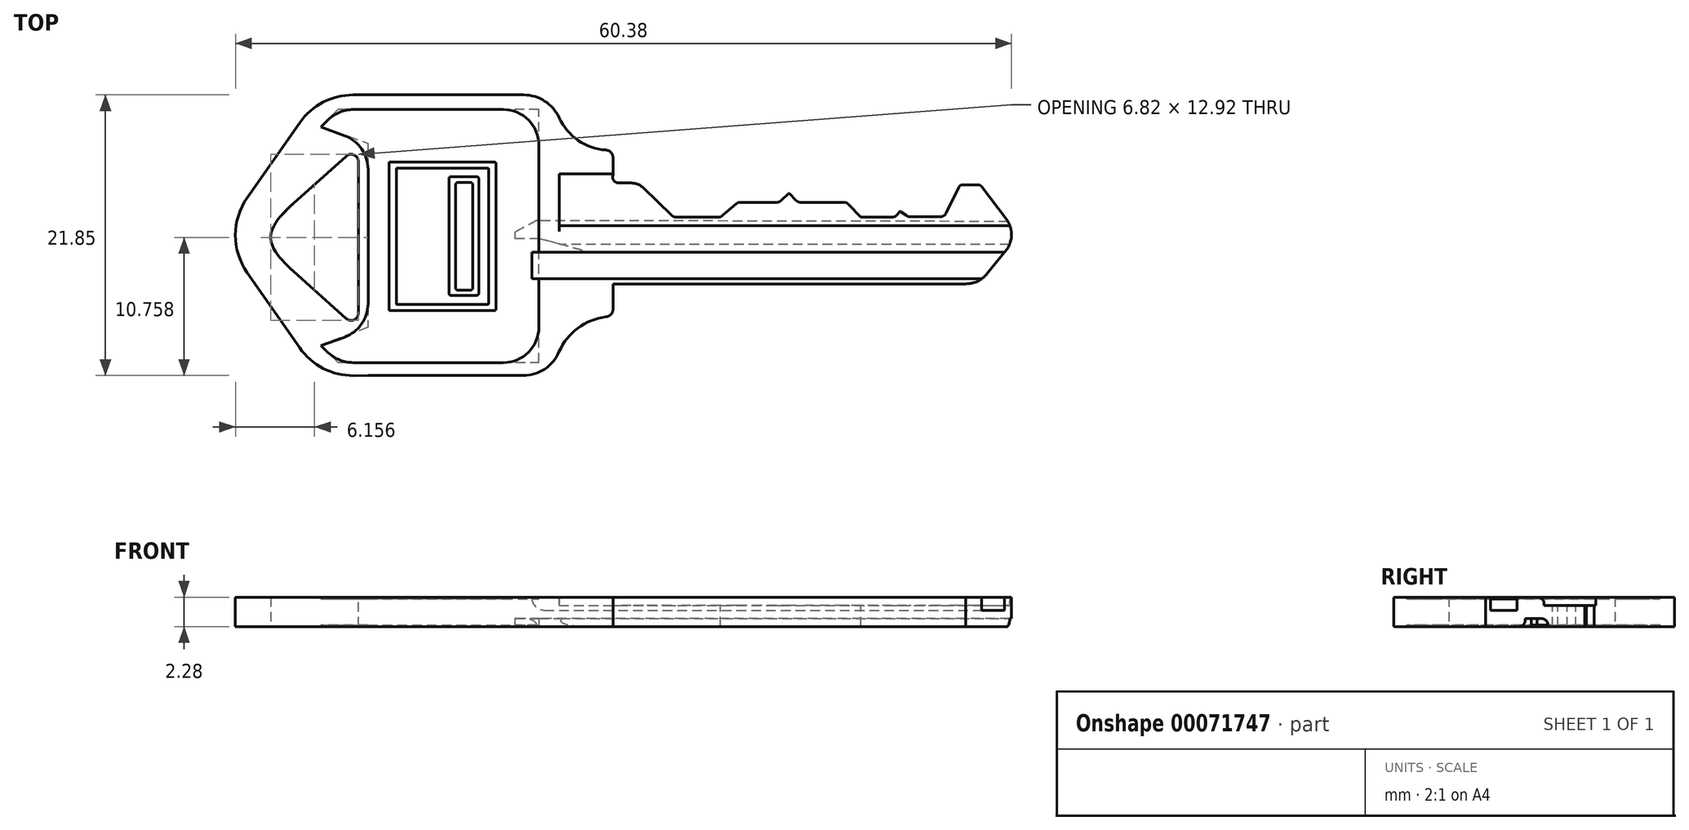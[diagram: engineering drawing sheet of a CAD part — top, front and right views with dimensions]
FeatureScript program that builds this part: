
annotation { "Feature Type Name" : "Feature", "Feature Type Description" : "" }
export const myFeature = defineFeature(function(context is Context, id is Id, definition is map)
    precondition{}
    {
        {
            var Q0;
            Q0=qCreatedBy(makeId("Top.planeOp"),FACE);
            var sketch = newSketch(context, id + "F0", { "sketchPlane" : qUnion([Q0])});
            skLineSegment(sketch, "E0.bottom", {"start": v(-49.06, 40.34) * mm, "end": v(-34.58, 40.34) * mm});
            skLineSegment(sketch, "E0.top", {"start": v(-49.06, 18.5) * mm, "end": v(-34.58, 18.5) * mm});
            skLineSegment(sketch, "E0.left", {"start": v(-49.06, 40.34) * mm, "end": v(-49.06, 18.5) * mm});
            skLineSegment(sketch, "E0.right", {"start": v(-34.58, 40.34) * mm, "end": v(-34.58, 18.5) * mm});
            skLineSegment(sketch, "E1.bottom", {"start": v(-34.58, 33.5) * mm, "end": v(-2.57, 33.5) * mm});
            skLineSegment(sketch, "E1.top", {"start": v(-34.58, 25.63) * mm, "end": v(-2.57, 25.63) * mm});
            skLineSegment(sketch, "E1.left", {"start": v(-34.58, 33.5) * mm, "end": v(-34.58, 25.63) * mm});
            skLineSegment(sketch, "E1.right", {"start": v(-2.57, 33.5) * mm, "end": v(-2.57, 25.63) * mm});
            skLineSegment(sketch, "E2.bottom", {"start": v(-34.58, 36.05) * mm, "end": v(-30, 36.05) * mm});
            skLineSegment(sketch, "E2.top", {"start": v(-34.58, 23.1) * mm, "end": v(-30, 23.1) * mm});
            skLineSegment(sketch, "E2.left", {"start": v(-34.58, 36.05) * mm, "end": v(-34.58, 23.1) * mm});
            skLineSegment(sketch, "E2.right", {"start": v(-30, 36.05) * mm, "end": v(-30, 23.1) * mm});
            skArc(sketch, "E3", {"start": v(-34.58, 40.34) * mm, "mid": v(-33.22, 37.2) * mm, "end": v(-30, 36.05) * mm});
            skArc(sketch, "E4", {"start": v(-30, 23.1) * mm, "mid": v(-33.25, 21.74) * mm, "end": v(-34.58, 18.5) * mm});
            skPoint(sketch, "E5", {"position": v(-30, 33.5) * mm});
            skPoint(sketch, "E6", {"position": v(-30, 25.63) * mm});
            skLineSegment(sketch, "E7", {"start": v(-49.06, 29.42) * mm, "end": v(-2.57, 29.42) * mm});
            skPoint(sketch, "E8", {"position": v(-30, 29.42) * mm});
            skLineSegment(sketch, "E9", {"start": v(-49.06, 40.34) * mm, "end": v(-52.87, 40.34) * mm});
            skLineSegment(sketch, "E10", {"start": v(-52.87, 40.34) * mm, "end": v(-60.5, 29.42) * mm});
            skLineSegment(sketch, "E11", {"start": v(-60.5, 29.42) * mm, "end": v(-52.87, 18.47) * mm});
            skLineSegment(sketch, "E12", {"start": v(-52.87, 18.47) * mm, "end": v(-49.06, 18.5) * mm});
            skLineSegment(sketch, "E13", {"start": v(-2.57, 33.5) * mm, "end": v(-1.57, 33.5) * mm});
            skLineSegment(sketch, "E14", {"start": v(-1.57, 33.5) * mm, "end": v(1.56, 29.42) * mm});
            skLineSegment(sketch, "E15", {"start": v(1.56, 29.42) * mm, "end": v(-1.57, 25.62) * mm});
            skLineSegment(sketch, "E16", {"start": v(-1.57, 25.62) * mm, "end": v(-2.57, 25.63) * mm});
            skSolve(sketch);
        }
        {
            var Q0;
            Q0=makeQuery(id+"F0.imprint","IMPRINT",FACE,{"disambiguationData":[TD([[makeQuery(id+"F0.imprint","IMPRINT",EDGE,{"derivedFrom":sQuery(id+"F0.wireOp",EDGE,"E1.bottom")}),-1.0]])]});
            var Q1;
            {var subQ0=sQuery(id+"F0.wireOp",EDGE,"E3");var subQ3=sQuery(id+"F0.wireOp",EDGE,"E2.bottom");var subQ5=makeQuery(id+"F0.imprint","INTERSECT",VERTEX,{"derivedFrom":[subQ3,subQ0]});Q1=makeQuery(id+"F0.imprint","IMPRINT",FACE,{"disambiguationData":[TD([[makeQuery(id+"F0.imprint","IMPRINT",EDGE,{"disambiguationData":[TD([[subQ5,1.0]])],"derivedFrom":subQ3}),1.0]])]});}
            var Q2;
            {var subQ4=sQuery(id+"F0.wireOp",EDGE,"E1.bottom");var subQ6=sQuery(id+"F0.wireOp",EDGE,"E2.left");var subQ7=makeQuery(id+"F0.imprint","INTERSECT",VERTEX,{"derivedFrom":[subQ4,subQ6]});Q2=makeQuery(id+"F0.imprint","IMPRINT",FACE,{"disambiguationData":[TD([[makeQuery(id+"F0.imprint","IMPRINT",EDGE,{"disambiguationData":[TD([[subQ7,-1.0]])],"derivedFrom":subQ4}),1.0]])]});}
            var Q3;
            {var subQ5=sQuery(id+"F0.wireOp",EDGE,"E2.top");Q3=makeQuery(id+"F0.imprint","IMPRINT",FACE,{"disambiguationData":[TD([[makeQuery(id+"F0.imprint","IMPRINT",EDGE,{"derivedFrom":subQ5}),1.0]])]});}
            var Q4;
            {var subQ0=sQuery(id+"F0.wireOp",EDGE,"E2.top");Q4=makeQuery(id+"F0.imprint","IMPRINT",FACE,{"disambiguationData":[TD([[makeQuery(id+"F0.imprint","IMPRINT",EDGE,{"derivedFrom":subQ0}),-1.0]])]});}
            var Q5;
            {var subQ0=sQuery(id+"F0.wireOp",EDGE,"3a7dfe4d-6823-4ebe-8630-0b1af203f991.3");Q5=makeQuery(id+"F0.imprint","IMPRINT",FACE,{"disambiguationData":[TD([[makeQuery(id+"F0.imprint","IMPRINT",EDGE,{"derivedFrom":subQ0}),1.0]])]});}
            var Q6;
            {var subQ0=sQuery(id+"F0.wireOp",EDGE,"E0.left");Q6=makeQuery(id+"F0.imprint","IMPRINT",FACE,{"disambiguationData":[TD([[makeQuery(id+"F0.imprint","IMPRINT",EDGE,{"derivedFrom":subQ0}),-1.0]])]});}
            var Q7;
            {var subQ4=sQuery(id+"F0.wireOp",EDGE,"E0.left");Q7=makeQuery(id+"F0.imprint","IMPRINT",FACE,{"disambiguationData":[TD([[makeQuery(id+"F0.imprint","IMPRINT",EDGE,{"derivedFrom":subQ4}),1.0]])]});}
            var Q8;
            {var subQ9=sQuery(id+"F0.wireOp",EDGE,"E0.top");Q8=makeQuery(id+"F0.imprint","IMPRINT",FACE,{"disambiguationData":[TD([[makeQuery(id+"F0.imprint","IMPRINT",EDGE,{"derivedFrom":subQ9}),1.0]])]});}
            var Q9;
            {var subQ0=sQuery(id+"F0.wireOp",EDGE,"E2.left");var subQ1=sQuery(id+"F0.wireOp",EDGE,"E1.top");var subQ2=makeQuery(id+"F0.imprint","INTERSECT",VERTEX,{"derivedFrom":[subQ1,subQ0]});Q9=makeQuery(id+"F0.imprint","IMPRINT",FACE,{"disambiguationData":[TD([[makeQuery(id+"F0.imprint","IMPRINT",EDGE,{"disambiguationData":[TD([[subQ2,-1.0]])],"derivedFrom":subQ1}),1.0]])]});}
            var Q10;
            {var subQ0=sQuery(id+"F0.wireOp",EDGE,"E1.right");var subQ1=sQuery(id+"F0.wireOp",EDGE,"E1.top");var subQ2=makeQuery(id+"F0.imprint","INTERSECT",VERTEX,{"derivedFrom":[subQ1,subQ0]});Q10=makeQuery(id+"F0.imprint","IMPRINT",FACE,{"disambiguationData":[TD([[makeQuery(id+"F0.imprint","IMPRINT",EDGE,{"disambiguationData":[TD([[subQ2,1.0]])],"derivedFrom":subQ1}),1.0]])]});}
            var Q11;
            {var subQ3=sQuery(id+"F0.wireOp",EDGE,"E13");Q11=makeQuery(id+"F0.imprint","IMPRINT",FACE,{"disambiguationData":[TD([[makeQuery(id+"F0.imprint","IMPRINT",EDGE,{"derivedFrom":subQ3}),-1.0]])]});}
            extrude(context, id + "F1", {"entities" : qUnion([Q0, Q1, Q2, Q3, Q4, Q5, Q6, Q7, Q8, Q9, Q10, Q11]), "endBound" : BoundingType.SYMMETRIC, "depth" : 2.3 * mm});
        }
        {
            var Q0;
            Q0=makeQuery(id+"F1.opExtrude","CAP_FACE",FACE,{"disambiguationData":[OSD([sQuery(id+"F0.wireOp",EDGE,"E0.bottom"),sQuery(id+"F0.wireOp",EDGE,"E0.top"),sQuery(id+"F0.wireOp",EDGE,"E1.bottom"),sQuery(id+"F0.wireOp",EDGE,"E1.top"),sQuery(id+"F0.wireOp",EDGE,"E1.right"),sQuery(id+"F0.wireOp",EDGE,"E2.right"),sQuery(id+"F0.wireOp",EDGE,"E3"),sQuery(id+"F0.wireOp",EDGE,"E4"),sQuery(id+"F0.wireOp",EDGE,"E9"),sQuery(id+"F0.wireOp",EDGE,"E10"),sQuery(id+"F0.wireOp",EDGE,"E11"),sQuery(id+"F0.wireOp",EDGE,"E12")])],"isStart":false});
            var sketch = newSketch(context, id + "F2", { "sketchPlane" : qUnion([Q0])});
            skLineSegment(sketch, "E17", {"start": v(-57.81, 29.25) * mm, "end": v(-49.81, 22.07) * mm});
            skLineSegment(sketch, "E18", {"start": v(-49.81, 22.07) * mm, "end": v(-49.81, 36.43) * mm});
            skLineSegment(sketch, "E19", {"start": v(-49.81, 36.43) * mm, "end": v(-57.81, 29.25) * mm});
            skPoint(sketch, "E20", {"position": v(-49.81, 29.25) * mm});
            skSolve(sketch);
        }
        {
            var Q0;
            Q0=makeQuery(id+"F1.opExtrude","SWEPT_EDGE",EDGE,{"disambiguationData":[OSD([sQuery(id+"F0.wireOp",EDGE,"E11"),sQuery(id+"F0.wireOp",EDGE,"E12")])]});
            var Q1;
            Q1=makeQuery(id+"F1.opExtrude","SWEPT_EDGE",EDGE,{"disambiguationData":[OSD([sQuery(id+"F0.wireOp",EDGE,"E9"),sQuery(id+"F0.wireOp",EDGE,"E10")])]});
            var Q2;
            Q2=makeQuery(id+"F1.opExtrude","SWEPT_EDGE",EDGE,{"disambiguationData":[OSD([sQuery(id+"F0.wireOp",EDGE,"E10"),sQuery(id+"F0.wireOp",EDGE,"E11")])]});
            fillet(context, id + "F3", {"entities" : qUnion([Q0, Q1, Q2]), "radius" : 5.08 * mm, "tangentPropagation" : true, "allowEdgeOverflow" : false});
        }
        {
            var Q0;
            Q0=makeQuery(id+"F1.opExtrude","SWEPT_EDGE",EDGE,{"disambiguationData":[OSD([sQuery(id+"F0.wireOp",EDGE,"E0.bottom"),sQuery(id+"F0.wireOp",EDGE,"E0.right"),sQuery(id+"F0.wireOp",EDGE,"E3")])]});
            var Q1;
            Q1=makeQuery(id+"F1.opExtrude","SWEPT_EDGE",EDGE,{"disambiguationData":[OSD([sQuery(id+"F0.wireOp",EDGE,"E0.top"),sQuery(id+"F0.wireOp",EDGE,"E0.right"),sQuery(id+"F0.wireOp",EDGE,"E4")])]});
            fillet(context, id + "F4", {"entities" : qUnion([Q0, Q1]), "radius" : 3.05 * mm, "tangentPropagation" : true, "allowEdgeOverflow" : false});
        }
        {
            var Q0;
            Q0=makeQuery(id+"F1.opExtrude","SWEPT_EDGE",EDGE,{"disambiguationData":[OSD([sQuery(id+"F0.wireOp",EDGE,"E2.bottom"),sQuery(id+"F0.wireOp",EDGE,"E2.right"),sQuery(id+"F0.wireOp",EDGE,"E3")])]});
            var Q1;
            Q1=makeQuery(id+"F1.opExtrude","SWEPT_EDGE",EDGE,{"disambiguationData":[OSD([sQuery(id+"F0.wireOp",EDGE,"E2.top"),sQuery(id+"F0.wireOp",EDGE,"E2.right"),sQuery(id+"F0.wireOp",EDGE,"E4")])]});
            fillet(context, id + "F5", {"entities" : qUnion([Q0, Q1]), "radius" : 0.6 * mm, "tangentPropagation" : true, "allowEdgeOverflow" : false});
        }
        {
            var Q0;
            Q0=makeQuery(id+"F2.imprint","IMPRINT",FACE,{"disambiguationData":[TD([[makeQuery(id+"F2.imprint","IMPRINT",EDGE,{"derivedFrom":sQuery(id+"F2.wireOp",EDGE,"E17")}),1.0]])]});
            extrude(context, id + "F6", {"entities" : qUnion([Q0]), "operationType" : NewBodyOperationType.REMOVE, "endBound" : BoundingType.THROUGH_ALL, "oppositeDirection" : true, "depth" : 9.1 * mm});
        }
        {
            var Q0;
            Q0=makeQuery(id+"F6.boolean.opBoolean","COPY",EDGE,{"derivedFrom":makeQuery(id+"F6.opExtrude","SWEPT_EDGE",EDGE,{"disambiguationData":[OSD([sQuery(id+"F2.wireOp",EDGE,"E17"),sQuery(id+"F2.wireOp",EDGE,"E18")])]})});
            var Q1;
            Q1=makeQuery(id+"F6.boolean.opBoolean","COPY",EDGE,{"derivedFrom":makeQuery(id+"F6.opExtrude","SWEPT_EDGE",EDGE,{"disambiguationData":[OSD([sQuery(id+"F2.wireOp",EDGE,"E18"),sQuery(id+"F2.wireOp",EDGE,"E19")])]})});
            fillet(context, id + "F7", {"entities" : qUnion([Q0, Q1]), "radius" : 0.58 * mm, "tangentPropagation" : true, "allowEdgeOverflow" : false});
        }
        {
            var Q0;
            Q0=makeQuery(id+"F6.boolean.opBoolean","COPY",EDGE,{"derivedFrom":makeQuery(id+"F6.opExtrude","SWEPT_EDGE",EDGE,{"disambiguationData":[OSD([sQuery(id+"F2.wireOp",EDGE,"E17"),sQuery(id+"F2.wireOp",EDGE,"E19")])]})});
            fillet(context, id + "F8", {"entities" : qUnion([Q0]), "radius" : 3.55 * mm, "tangentPropagation" : true, "rho" : .6, "crossSection" : FilletCrossSection.CONIC, "allowEdgeOverflow" : false});
        }
        {
            var Q0;
            Q0=makeQuery(id+"F2.imprint","IMPRINT",FACE,{"disambiguationData":[TD([[makeQuery(id+"F2.imprint","IMPRINT",EDGE,{"derivedFrom":sQuery(id+"F2.wireOp",EDGE,"E17")}),-1.0]])]});
            var sketch = newSketch(context, id + "F9", { "sketchPlane" : qUnion([Q0])});
            skLineSegment(sketch, "E21", {"start": v(-49.06, 29.42) * mm, "end": v(-49.06, 36.47) * mm});
            skLineSegment(sketch, "E22", {"start": v(-49.06, 36.47) * mm, "end": v(-52.73, 37.84) * mm});
            skLineSegment(sketch, "E23", {"start": v(-52.73, 37.84) * mm, "end": v(-51.36, 39.2) * mm});
            skLineSegment(sketch, "E24", {"start": v(-51.36, 39.2) * mm, "end": v(-35.77, 39.2) * mm});
            skLineSegment(sketch, "E25", {"start": v(-35.77, 39.2) * mm, "end": v(-35.77, 19.5) * mm});
            skLineSegment(sketch, "E26", {"start": v(-35.77, 19.5) * mm, "end": v(-51.36, 19.5) * mm});
            skLineSegment(sketch, "E27", {"start": v(-51.36, 19.5) * mm, "end": v(-52.73, 20.83) * mm});
            skLineSegment(sketch, "E28", {"start": v(-52.73, 20.83) * mm, "end": v(-49.06, 22.13) * mm});
            skLineSegment(sketch, "E29", {"start": v(-49.06, 22.13) * mm, "end": v(-49.06, 29.42) * mm});
            skLineSegment(sketch, "E30.bottom", {"start": v(-36.33, 28.08) * mm, "end": v(0.92, 28.08) * mm});
            skLineSegment(sketch, "E30.top", {"start": v(-36.33, 26.03) * mm, "end": v(0.92, 26.03) * mm});
            skLineSegment(sketch, "E30.left", {"start": v(-36.33, 28.08) * mm, "end": v(-36.33, 26.03) * mm});
            skLineSegment(sketch, "E30.right", {"start": v(0.92, 28.08) * mm, "end": v(0.92, 26.03) * mm});
            skLineSegment(sketch, "E31.bottom", {"start": v(-34.2, 34.2) * mm, "end": v(3.04, 34.2) * mm});
            skLineSegment(sketch, "E31.top", {"start": v(-34.2, 30.17) * mm, "end": v(3.04, 30.17) * mm});
            skLineSegment(sketch, "E31.left", {"start": v(-34.2, 34.2) * mm, "end": v(-34.2, 30.17) * mm});
            skLineSegment(sketch, "E31.right", {"start": v(3.04, 34.2) * mm, "end": v(3.04, 30.17) * mm});
            skSolve(sketch);
        }
        {
            var Q0;
            Q0=makeQuery(id+"F1.opExtrude","CAP_FACE",FACE,{"disambiguationData":[OSD([sQuery(id+"F0.wireOp",EDGE,"E0.bottom"),sQuery(id+"F0.wireOp",EDGE,"E0.top"),sQuery(id+"F0.wireOp",EDGE,"E1.bottom"),sQuery(id+"F0.wireOp",EDGE,"E1.top"),sQuery(id+"F0.wireOp",EDGE,"E2.right"),sQuery(id+"F0.wireOp",EDGE,"E3"),sQuery(id+"F0.wireOp",EDGE,"E4"),sQuery(id+"F0.wireOp",EDGE,"E9"),sQuery(id+"F0.wireOp",EDGE,"E10"),sQuery(id+"F0.wireOp",EDGE,"E11"),sQuery(id+"F0.wireOp",EDGE,"E12"),sQuery(id+"F0.wireOp",EDGE,"E13"),sQuery(id+"F0.wireOp",EDGE,"E14"),sQuery(id+"F0.wireOp",EDGE,"E15"),sQuery(id+"F0.wireOp",EDGE,"E16")])],"isStart":true});
            var sketch = newSketch(context, id + "F10", { "sketchPlane" : qUnion([Q0])});
            skLineSegment(sketch, "E32", {"start": v(-49.08, -22.24) * mm, "end": v(-49.08, -19.13) * mm});
            skLineSegment(sketch, "E33", {"start": v(-49.08, -22.24) * mm, "end": v(-52.74, -20.87) * mm});
            skLineSegment(sketch, "E34", {"start": v(-52.74, -20.87) * mm, "end": v(-51.38, -19.51) * mm});
            skLineSegment(sketch, "E35", {"start": v(-51.38, -19.51) * mm, "end": v(-35.78, -19.51) * mm});
            skLineSegment(sketch, "E36", {"start": v(-35.78, -19.51) * mm, "end": v(-35.78, -39.2) * mm});
            skLineSegment(sketch, "E37", {"start": v(-35.78, -39.2) * mm, "end": v(-51.38, -39.2) * mm});
            skLineSegment(sketch, "E38", {"start": v(-51.38, -39.2) * mm, "end": v(-52.74, -37.88) * mm});
            skLineSegment(sketch, "E39", {"start": v(-52.74, -37.88) * mm, "end": v(-49.08, -36.58) * mm});
            skLineSegment(sketch, "E40", {"start": v(-49.08, -36.58) * mm, "end": v(-49.08, -19.13) * mm});
            skLineSegment(sketch, "E41", {"start": v(-35.64, -30.58) * mm, "end": v(-35.92, -30.58) * mm});
            skLineSegment(sketch, "E42", {"start": v(-35.92, -30.58) * mm, "end": v(-37.64, -29.65) * mm});
            skLineSegment(sketch, "E43", {"start": v(-37.64, -29.65) * mm, "end": v(-37.64, -29.19) * mm});
            skLineSegment(sketch, "E44", {"start": v(-37.64, -29.19) * mm, "end": v(-35.78, -29.19) * mm});
            skLineSegment(sketch, "E45", {"start": v(-35.78, -29.19) * mm, "end": v(-34.07, -28.7) * mm});
            skLineSegment(sketch, "E46", {"start": v(-34.07, -28.7) * mm, "end": v(2.33, -28.7) * mm});
            skLineSegment(sketch, "E47", {"start": v(2.33, -28.7) * mm, "end": v(2.33, -30.5) * mm});
            skLineSegment(sketch, "E48", {"start": v(2.33, -30.5) * mm, "end": v(-35.64, -30.58) * mm});
            skSolve(sketch);
        }
        {
            var Q0;
            Q0=makeQuery(id+"F9.imprint","IMPRINT",FACE,{"disambiguationData":[TD([[makeQuery(id+"F9.imprint","IMPRINT",EDGE,{"derivedFrom":sQuery(id+"F9.wireOp",EDGE,"E21")}),-1.0]])]});
            var Q1;
            {var subQ4=sQuery(id+"F10.wireOp",EDGE,"E37");Q1=makeQuery(id+"F10.imprint","IMPRINT",FACE,{"disambiguationData":[TD([[makeQuery(id+"F10.imprint","IMPRINT",EDGE,{"derivedFrom":subQ4}),-1.0]])]});}
            var Q2;
            {var subQ0=sQuery(id+"F10.wireOp",EDGE,"E33");Q2=makeQuery(id+"F10.imprint","IMPRINT",FACE,{"disambiguationData":[TD([[makeQuery(id+"F10.imprint","IMPRINT",EDGE,{"derivedFrom":subQ0}),-1.0]])]});}
            extrude(context, id + "F11", {"entities" : qUnion([Q0, Q1, Q2]), "operationType" : NewBodyOperationType.REMOVE, "endBound" : BoundingType.SYMMETRIC, "oppositeDirection" : true, "depth" : 0.25 * mm});
        }
        {
            var Q0;
            Q0=makeQuery(id+"F11.boolean.opBoolean","COPY",EDGE,{"derivedFrom":makeQuery(id+"F11.opExtrude","SWEPT_EDGE",EDGE,{"disambiguationData":[OSD([sQuery(id+"F9.wireOp",EDGE,"E28"),sQuery(id+"F9.wireOp",EDGE,"E29")])]})});
            var Q1;
            Q1=makeQuery(id+"F11.boolean.opBoolean","COPY",EDGE,{"derivedFrom":makeQuery(id+"F11.opExtrude","SWEPT_EDGE",EDGE,{"disambiguationData":[OSD([sQuery(id+"F9.wireOp",EDGE,"E21"),sQuery(id+"F9.wireOp",EDGE,"E22")])]})});
            var Q2;
            Q2=makeQuery(id+"F11.boolean.opBoolean","COPY",EDGE,{"derivedFrom":makeQuery(id+"F11.opExtrude","SWEPT_EDGE",EDGE,{"disambiguationData":[OSD([sQuery(id+"F9.wireOp",EDGE,"E25"),sQuery(id+"F9.wireOp",EDGE,"E26")])]})});
            var Q3;
            Q3=makeQuery(id+"F11.boolean.opBoolean","COPY",EDGE,{"derivedFrom":makeQuery(id+"F11.opExtrude","SWEPT_EDGE",EDGE,{"disambiguationData":[OSD([sQuery(id+"F9.wireOp",EDGE,"E24"),sQuery(id+"F9.wireOp",EDGE,"E25")])]})});
            var Q4;
            Q4=makeQuery(id+"F11.boolean.opBoolean","COPY",EDGE,{"derivedFrom":makeQuery(id+"F11.opExtrude","SWEPT_EDGE",EDGE,{"disambiguationData":[OSD([sQuery(id+"F9.wireOp",EDGE,"E26"),sQuery(id+"F9.wireOp",EDGE,"E27")])]})});
            var Q5;
            Q5=makeQuery(id+"F11.boolean.opBoolean","COPY",EDGE,{"derivedFrom":makeQuery(id+"F11.opExtrude","SWEPT_EDGE",EDGE,{"disambiguationData":[OSD([sQuery(id+"F9.wireOp",EDGE,"E23"),sQuery(id+"F9.wireOp",EDGE,"E24")])]})});
            fillet(context, id + "F12", {"entities" : qUnion([Q0, Q1, Q2, Q3, Q4, Q5]), "radius" : 2.8 * mm, "tangentPropagation" : true, "allowEdgeOverflow" : false});
        }
        {
            var Q0;
            Q0=makeQuery(id+"F1.opExtrude","SWEPT_EDGE",EDGE,{"disambiguationData":[OSD([sQuery(id+"F0.wireOp",EDGE,"E15"),sQuery(id+"F0.wireOp",EDGE,"E16")])]});
            var Q1;
            Q1=makeQuery(id+"F1.opExtrude","SWEPT_EDGE",EDGE,{"disambiguationData":[OSD([sQuery(id+"F0.wireOp",EDGE,"E14"),sQuery(id+"F0.wireOp",EDGE,"E15")])]});
            fillet(context, id + "F13", {"entities" : qUnion([Q0, Q1]), "radius" : 2.05 * mm, "tangentPropagation" : true, "allowEdgeOverflow" : false});
        }
        {
            var Q0;
            {var subQ1=sQuery(id+"F9.wireOp",EDGE,"E31.top");Q0=makeQuery(id+"F9.imprint","IMPRINT",FACE,{"disambiguationData":[TD([[makeQuery(id+"F9.imprint","IMPRINT",EDGE,{"derivedFrom":subQ1}),1.0]])]});}
            extrude(context, id + "F14", {"entities" : qUnion([Q0]), "operationType" : NewBodyOperationType.REMOVE, "endBound" : BoundingType.SYMMETRIC, "oppositeDirection" : true, "depth" : 1.27 * mm});
        }
        {
            var Q0;
            {var subQ4=sQuery(id+"F10.wireOp",EDGE,"E42");Q0=makeQuery(id+"F10.imprint","IMPRINT",FACE,{"disambiguationData":[TD([[makeQuery(id+"F10.imprint","IMPRINT",EDGE,{"derivedFrom":subQ4}),-1.0]])]});}
            var Q1;
            {var subQ1=sQuery(id+"F10.wireOp",EDGE,"E45");Q1=makeQuery(id+"F10.imprint","IMPRINT",FACE,{"disambiguationData":[TD([[makeQuery(id+"F10.imprint","IMPRINT",EDGE,{"derivedFrom":subQ1}),-1.0]])]});}
            extrude(context, id + "F15", {"entities" : qUnion([Q0, Q1]), "operationType" : NewBodyOperationType.REMOVE, "endBound" : BoundingType.SYMMETRIC, "oppositeDirection" : true, "depth" : 1.27 * mm});
        }
        {
            var Q0;
            {var subQ0=sQuery(id+"F9.wireOp",EDGE,"E30.bottom");var subQ1=sQuery(id+"F9.wireOp",EDGE,"E25");var subQ2=makeQuery(id+"F9.imprint","INTERSECT",VERTEX,{"derivedFrom":[subQ1,subQ0]});Q0=makeQuery(id+"F9.imprint","IMPRINT",FACE,{"disambiguationData":[TD([[makeQuery(id+"F9.imprint","IMPRINT",EDGE,{"disambiguationData":[TD([[subQ2,-1.0]])],"derivedFrom":subQ1}),1.0]])]});}
            var Q1;
            {var subQ5=sQuery(id+"F9.wireOp",EDGE,"E30.left");Q1=makeQuery(id+"F9.imprint","IMPRINT",FACE,{"disambiguationData":[TD([[makeQuery(id+"F9.imprint","IMPRINT",EDGE,{"derivedFrom":subQ5}),1.0]])]});}
            var Q2;
            {var subQ0=sQuery(id+"F9.wireOp",EDGE,"E30.right");Q2=makeQuery(id+"F9.imprint","IMPRINT",FACE,{"disambiguationData":[TD([[makeQuery(id+"F9.imprint","IMPRINT",EDGE,{"derivedFrom":subQ0}),-1.0]])]});}
            extrude(context, id + "F16", {"entities" : qUnion([Q0, Q1, Q2]), "operationType" : NewBodyOperationType.REMOVE, "endBound" : BoundingType.SYMMETRIC, "oppositeDirection" : true, "depth" : 2.03 * mm});
        }
        {
            var Q0;
            Q0=makeQuery(id+"F16.boolean.opBoolean","COPY",EDGE,{"derivedFrom":makeQuery(id+"F16.opExtrude","CAP_EDGE",EDGE,{"disambiguationData":[OSD([sQuery(id+"F9.wireOp",EDGE,"E30.left")])],"isStart":false})});
            fillet(context, id + "F17", {"entities" : qUnion([Q0]), "radius" : 0.99 * mm, "tangentPropagation" : true, "allowEdgeOverflow" : false});
        }
        {
            var Q0;
            Q0=makeQuery(id+"F14.boolean.opBoolean","INTERSECT",EDGE,{"derivedFrom":[makeQuery(id+"F1.opExtrude","CAP_FACE",FACE,{"disambiguationData":[OSD([sQuery(id+"F0.wireOp",EDGE,"E0.bottom"),sQuery(id+"F0.wireOp",EDGE,"E0.top"),sQuery(id+"F0.wireOp",EDGE,"E1.bottom"),sQuery(id+"F0.wireOp",EDGE,"E1.top"),sQuery(id+"F0.wireOp",EDGE,"E2.right"),sQuery(id+"F0.wireOp",EDGE,"E3"),sQuery(id+"F0.wireOp",EDGE,"E4"),sQuery(id+"F0.wireOp",EDGE,"E9"),sQuery(id+"F0.wireOp",EDGE,"E10"),sQuery(id+"F0.wireOp",EDGE,"E11"),sQuery(id+"F0.wireOp",EDGE,"E12"),sQuery(id+"F0.wireOp",EDGE,"E13"),sQuery(id+"F0.wireOp",EDGE,"E14"),sQuery(id+"F0.wireOp",EDGE,"E15"),sQuery(id+"F0.wireOp",EDGE,"E16")])],"isStart":false}),makeQuery(id+"F14.opExtrude","SWEPT_FACE",FACE,{"disambiguationData":[OSD([sQuery(id+"F9.wireOp",EDGE,"E31.top")])]})]});
            var Q1;
            Q1=makeQuery(id+"F15.boolean.opBoolean","INTERSECT",EDGE,{"derivedFrom":[makeQuery(id+"F1.opExtrude","CAP_FACE",FACE,{"disambiguationData":[OSD([sQuery(id+"F0.wireOp",EDGE,"E0.bottom"),sQuery(id+"F0.wireOp",EDGE,"E0.top"),sQuery(id+"F0.wireOp",EDGE,"E1.bottom"),sQuery(id+"F0.wireOp",EDGE,"E1.top"),sQuery(id+"F0.wireOp",EDGE,"E2.right"),sQuery(id+"F0.wireOp",EDGE,"E3"),sQuery(id+"F0.wireOp",EDGE,"E4"),sQuery(id+"F0.wireOp",EDGE,"E9"),sQuery(id+"F0.wireOp",EDGE,"E10"),sQuery(id+"F0.wireOp",EDGE,"E11"),sQuery(id+"F0.wireOp",EDGE,"E12"),sQuery(id+"F0.wireOp",EDGE,"E13"),sQuery(id+"F0.wireOp",EDGE,"E14"),sQuery(id+"F0.wireOp",EDGE,"E15"),sQuery(id+"F0.wireOp",EDGE,"E16")])],"isStart":true}),makeQuery(id+"F15.opExtrude","SWEPT_FACE",FACE,{"disambiguationData":[OSD([sQuery(id+"F10.wireOp",EDGE,"E46")])]})]});
            fillet(context, id + "F18", {"entities" : qUnion([Q0, Q1]), "radius" : 0.47 * mm, "tangentPropagation" : true, "allowEdgeOverflow" : false});
        }
        {
            var Q0;
            Q0=makeQuery(id+"F2.imprint","IMPRINT",FACE,{"disambiguationData":[TD([[makeQuery(id+"F2.imprint","IMPRINT",EDGE,{"derivedFrom":sQuery(id+"F2.wireOp",EDGE,"E17")}),-1.0]])]});
            var sketch = newSketch(context, id + "F19", { "sketchPlane" : qUnion([Q0])});
            skLineSegment(sketch, "E49", {"start": v(-1.26, 33.34) * mm, "end": v(-3, 33.34) * mm});
            skLineSegment(sketch, "E50", {"start": v(-3, 33.34) * mm, "end": v(-4.22, 30.86) * mm});
            skLineSegment(sketch, "E51", {"start": v(-4.22, 30.86) * mm, "end": v(-7.06, 30.86) * mm});
            skLineSegment(sketch, "E52", {"start": v(-7.06, 30.86) * mm, "end": v(-7.7, 31.3) * mm});
            skLineSegment(sketch, "E53", {"start": v(-7.7, 31.3) * mm, "end": v(-8.02, 30.83) * mm});
            skLineSegment(sketch, "E54", {"start": v(-8.02, 30.83) * mm, "end": v(-10.72, 30.83) * mm});
            skLineSegment(sketch, "E55", {"start": v(-10.72, 30.83) * mm, "end": v(-11.82, 31.97) * mm});
            skLineSegment(sketch, "E56", {"start": v(-11.82, 31.97) * mm, "end": v(-15.61, 31.97) * mm});
            skLineSegment(sketch, "E57", {"start": v(-15.61, 31.97) * mm, "end": v(-16.3, 32.7) * mm});
            skLineSegment(sketch, "E58", {"start": v(-16.3, 32.7) * mm, "end": v(-17.07, 31.97) * mm});
            skLineSegment(sketch, "E59", {"start": v(-17.07, 31.97) * mm, "end": v(-20.29, 31.97) * mm});
            skLineSegment(sketch, "E60", {"start": v(-20.29, 31.97) * mm, "end": v(-21.65, 30.83) * mm});
            skLineSegment(sketch, "E61", {"start": v(-21.65, 30.83) * mm, "end": v(-25.31, 30.83) * mm});
            skLineSegment(sketch, "E62", {"start": v(-25.31, 30.83) * mm, "end": v(-28.03, 33.48) * mm});
            skLineSegment(sketch, "E63", {"start": v(-28.03, 33.48) * mm, "end": v(-30.03, 33.48) * mm});
            skLineSegment(sketch, "E64", {"start": v(-30.03, 33.48) * mm, "end": v(-30.03, 34.07) * mm});
            skLineSegment(sketch, "E65", {"start": v(-30.03, 34.07) * mm, "end": v(-1.31, 34.07) * mm});
            skLineSegment(sketch, "E66", {"start": v(-1.31, 34.07) * mm, "end": v(-1.26, 33.34) * mm});
            skSolve(sketch);
        }
        {
            var Q0;
            Q0=qSketchRegion(id+"F19",true);
            extrude(context, id + "F20", {"entities" : qUnion([Q0]), "operationType" : NewBodyOperationType.REMOVE, "endBound" : BoundingType.THROUGH_ALL, "oppositeDirection" : true, "depth" : 25.4 * mm});
        }
        {
            var Q0;
            Q0=makeQuery(id+"F20.boolean.opBoolean","COPY",EDGE,{"derivedFrom":makeQuery(id+"F20.opExtrude","SWEPT_EDGE",EDGE,{"disambiguationData":[OSD([sQuery(id+"F19.wireOp",EDGE,"E63"),sQuery(id+"F19.wireOp",EDGE,"E64")])]})});
            var Q1;
            Q1=makeQuery(id+"F20.boolean.opBoolean","COPY",EDGE,{"derivedFrom":makeQuery(id+"F20.opExtrude","SWEPT_EDGE",EDGE,{"disambiguationData":[OSD([sQuery(id+"F19.wireOp",EDGE,"E59"),sQuery(id+"F19.wireOp",EDGE,"E60")])]})});
            var Q2;
            Q2=makeQuery(id+"F20.boolean.opBoolean","COPY",EDGE,{"derivedFrom":makeQuery(id+"F20.opExtrude","SWEPT_EDGE",EDGE,{"disambiguationData":[OSD([sQuery(id+"F19.wireOp",EDGE,"E55"),sQuery(id+"F19.wireOp",EDGE,"E56")])]})});
            var Q3;
            Q3=makeQuery(id+"F20.boolean.opBoolean","COPY",EDGE,{"derivedFrom":makeQuery(id+"F20.opExtrude","SWEPT_EDGE",EDGE,{"disambiguationData":[OSD([sQuery(id+"F19.wireOp",EDGE,"E51"),sQuery(id+"F19.wireOp",EDGE,"E52")])]})});
            var Q4;
            Q4=makeQuery(id+"F20.boolean.opBoolean","COPY",EDGE,{"derivedFrom":makeQuery(id+"F20.opExtrude","SWEPT_EDGE",EDGE,{"disambiguationData":[OSD([sQuery(id+"F19.wireOp",EDGE,"E53"),sQuery(id+"F19.wireOp",EDGE,"E54")])]})});
            var Q5;
            Q5=makeQuery(id+"F20.boolean.opBoolean","COPY",EDGE,{"derivedFrom":makeQuery(id+"F20.opExtrude","SWEPT_EDGE",EDGE,{"disambiguationData":[OSD([sQuery(id+"F19.wireOp",EDGE,"E50"),sQuery(id+"F19.wireOp",EDGE,"E51")])]})});
            var Q6;
            Q6=makeQuery(id+"F20.boolean.opBoolean","COPY",EDGE,{"derivedFrom":makeQuery(id+"F20.opExtrude","SWEPT_EDGE",EDGE,{"disambiguationData":[OSD([sQuery(id+"F19.wireOp",EDGE,"E58"),sQuery(id+"F19.wireOp",EDGE,"E59")])]})});
            var Q7;
            Q7=makeQuery(id+"F20.boolean.opBoolean","COPY",EDGE,{"derivedFrom":makeQuery(id+"F20.opExtrude","SWEPT_EDGE",EDGE,{"disambiguationData":[OSD([sQuery(id+"F19.wireOp",EDGE,"E56"),sQuery(id+"F19.wireOp",EDGE,"E57")])]})});
            var Q8;
            Q8=makeQuery(id+"F20.boolean.opBoolean","COPY",EDGE,{"derivedFrom":makeQuery(id+"F20.opExtrude","SWEPT_EDGE",EDGE,{"disambiguationData":[OSD([sQuery(id+"F19.wireOp",EDGE,"E61"),sQuery(id+"F19.wireOp",EDGE,"E62")])]})});
            fillet(context, id + "F21", {"entities" : qUnion([Q0, Q1, Q2, Q3, Q4, Q5, Q6, Q7, Q8]), "radius" : 0.5 * mm, "tangentPropagation" : true, "allowEdgeOverflow" : false});
        }
        {
            var Q0;
            Q0=makeQuery(id+"F20.boolean.opBoolean","COPY",EDGE,{"derivedFrom":makeQuery(id+"F20.opExtrude","SWEPT_EDGE",EDGE,{"disambiguationData":[OSD([sQuery(id+"F19.wireOp",EDGE,"E62"),sQuery(id+"F19.wireOp",EDGE,"E63")])]})});
            fillet(context, id + "F22", {"entities" : qUnion([Q0]), "radius" : 1.4 * mm, "tangentPropagation" : true, "allowEdgeOverflow" : false});
        }
        {
            var Q0;
            Q0=makeQuery(id+"F20.boolean.opBoolean","COPY",EDGE,{"derivedFrom":makeQuery(id+"F20.opExtrude","SWEPT_EDGE",EDGE,{"disambiguationData":[OSD([sQuery(id+"F19.wireOp",EDGE,"E49"),sQuery(id+"F19.wireOp",EDGE,"E50")])]})});
            var Q1;
            Q1=makeQuery(id+"F20.boolean.opBoolean","INTERSECT",EDGE,{"derivedFrom":[makeQuery(id+"F1.opExtrude","SWEPT_FACE",FACE,{"disambiguationData":[OSD([sQuery(id+"F0.wireOp",EDGE,"E14")])]}),makeQuery(id+"F20.opExtrude","SWEPT_FACE",FACE,{"disambiguationData":[OSD([sQuery(id+"F19.wireOp",EDGE,"E49")])]})]});
            fillet(context, id + "F23", {"entities" : qUnion([Q0, Q1]), "radius" : 0.36 * mm, "tangentPropagation" : true, "allowEdgeOverflow" : false});
        }
        {
            var Q0;
            Q0=makeQuery(id+"F20.boolean.opBoolean","COPY",EDGE,{"derivedFrom":makeQuery(id+"F20.opExtrude","SWEPT_EDGE",EDGE,{"disambiguationData":[OSD([sQuery(id+"F19.wireOp",EDGE,"E52"),sQuery(id+"F19.wireOp",EDGE,"E53")])]})});
            var Q1;
            Q1=makeQuery(id+"F20.boolean.opBoolean","COPY",EDGE,{"derivedFrom":makeQuery(id+"F20.opExtrude","SWEPT_EDGE",EDGE,{"disambiguationData":[OSD([sQuery(id+"F19.wireOp",EDGE,"E57"),sQuery(id+"F19.wireOp",EDGE,"E58")])]})});
            fillet(context, id + "F24", {"entities" : qUnion([Q0, Q1]), "radius" : 0.1 * mm, "tangentPropagation" : true, "allowEdgeOverflow" : false});
        }
        {
            var Q0;
            Q0=makeQuery(id+"F15.boolean.opBoolean","COPY",EDGE,{"derivedFrom":makeQuery(id+"F15.opExtrude","CAP_EDGE",EDGE,{"disambiguationData":[OSD([sQuery(id+"F10.wireOp",EDGE,"E48")])],"isStart":false})});
            fillet(context, id + "F25", {"entities" : qUnion([Q0]), "radius" : 0.58 * mm, "tangentPropagation" : true, "allowEdgeOverflow" : false});
        }
        {
            var Q0;
            Q0=makeQuery(id+"F9.imprint","IMPRINT",FACE,{"disambiguationData":[TD([[makeQuery(id+"F9.imprint","IMPRINT",EDGE,{"derivedFrom":sQuery(id+"F9.wireOp",EDGE,"E21")}),-1.0]])]});
            var sketch = newSketch(context, id + "F26", { "sketchPlane" : qUnion([Q0])});
            skLineSegment(sketch, "E67.bottom", {"start": v(-47.44, 23.56) * mm, "end": v(-39.12, 23.56) * mm});
            skLineSegment(sketch, "E67.top", {"start": v(-47.44, 35.1) * mm, "end": v(-39.12, 35.1) * mm});
            skLineSegment(sketch, "E67.left", {"start": v(-47.44, 23.56) * mm, "end": v(-47.44, 35.1) * mm});
            skLineSegment(sketch, "E67.right", {"start": v(-39.12, 23.56) * mm, "end": v(-39.12, 35.1) * mm});
            skLineSegment(sketch, "E68.bottom", {"start": v(-46.87, 24.02) * mm, "end": v(-39.69, 24.02) * mm});
            skLineSegment(sketch, "E68.top", {"start": v(-46.87, 34.64) * mm, "end": v(-39.69, 34.64) * mm});
            skLineSegment(sketch, "E68.left", {"start": v(-46.87, 24.02) * mm, "end": v(-46.87, 34.64) * mm});
            skLineSegment(sketch, "E68.right", {"start": v(-39.69, 24.02) * mm, "end": v(-39.69, 34.64) * mm});
            skLineSegment(sketch, "E69.bottom", {"start": v(-42.77, 24.74) * mm, "end": v(-40.46, 24.74) * mm});
            skLineSegment(sketch, "E69.top", {"start": v(-42.77, 33.97) * mm, "end": v(-40.46, 33.97) * mm});
            skLineSegment(sketch, "E69.left", {"start": v(-42.77, 24.74) * mm, "end": v(-42.77, 33.97) * mm});
            skLineSegment(sketch, "E69.right", {"start": v(-40.46, 24.74) * mm, "end": v(-40.46, 33.97) * mm});
            skLineSegment(sketch, "E70.bottom", {"start": v(-42.25, 25.15) * mm, "end": v(-40.92, 25.15) * mm});
            skLineSegment(sketch, "E70.top", {"start": v(-42.25, 33.51) * mm, "end": v(-40.92, 33.51) * mm});
            skLineSegment(sketch, "E70.left", {"start": v(-42.25, 25.15) * mm, "end": v(-42.25, 33.51) * mm});
            skLineSegment(sketch, "E70.right", {"start": v(-40.92, 25.15) * mm, "end": v(-40.92, 33.51) * mm});
            skSolve(sketch);
        }
        {
            var Q0;
            Q0=qSketchRegion(id+"F26",true);
            var Q1;
            Q1=makeQuery(id+"F26.imprint","IMPRINT",FACE,{"disambiguationData":[TD([[makeQuery(id+"F26.imprint","IMPRINT",EDGE,{"derivedFrom":sQuery(id+"F26.wireOp",EDGE,"E69.bottom")}),1.0]])]});
            var Q2;
            Q2=makeQuery(id+"F11.boolean.opBoolean","COPY",FACE,{"derivedFrom":makeQuery(id+"F11.opExtrude","CAP_FACE",FACE,{"disambiguationData":[OSD([sQuery(id+"F9.wireOp",EDGE,"E21"),sQuery(id+"F9.wireOp",EDGE,"E22"),sQuery(id+"F9.wireOp",EDGE,"E23"),sQuery(id+"F9.wireOp",EDGE,"E24"),sQuery(id+"F9.wireOp",EDGE,"E25"),sQuery(id+"F9.wireOp",EDGE,"E26"),sQuery(id+"F9.wireOp",EDGE,"E27"),sQuery(id+"F9.wireOp",EDGE,"E28"),sQuery(id+"F9.wireOp",EDGE,"E29"),sQuery(id+"F9.wireOp",EDGE,"E30.bottom"),sQuery(id+"F9.wireOp",EDGE,"E30.top"),sQuery(id+"F9.wireOp",EDGE,"E30.left")])],"isStart":false})});
            extrude(context, id + "F27", {"entities" : qUnion([Q0, Q1]), "operationType" : NewBodyOperationType.ADD, "endBound" : BoundingType.UP_TO_SURFACE, "oppositeDirection" : true, "endBoundEntityFace" : qUnion([Q2]), "depth" : 0.15 * mm});
        }
        {
            var Q0;
            Q0=makeQuery(id+"F27.opExtrude","SWEPT_EDGE",EDGE,{"disambiguationData":[OSD([sQuery(id+"F26.wireOp",EDGE,"E67.bottom"),sQuery(id+"F26.wireOp",EDGE,"E67.left")])]});
            var Q1;
            Q1=makeQuery(id+"F27.opExtrude","SWEPT_EDGE",EDGE,{"disambiguationData":[OSD([sQuery(id+"F26.wireOp",EDGE,"E67.top"),sQuery(id+"F26.wireOp",EDGE,"E67.left")])]});
            var Q2;
            Q2=makeQuery(id+"F27.opExtrude","SWEPT_EDGE",EDGE,{"disambiguationData":[OSD([sQuery(id+"F26.wireOp",EDGE,"E67.top"),sQuery(id+"F26.wireOp",EDGE,"E67.right")])]});
            var Q3;
            Q3=makeQuery(id+"F27.opExtrude","SWEPT_EDGE",EDGE,{"disambiguationData":[OSD([sQuery(id+"F26.wireOp",EDGE,"E67.bottom"),sQuery(id+"F26.wireOp",EDGE,"E67.right")])]});
            var Q4;
            Q4=makeQuery(id+"F27.opExtrude","SWEPT_EDGE",EDGE,{"disambiguationData":[OSD([sQuery(id+"F26.wireOp",EDGE,"E68.bottom"),sQuery(id+"F26.wireOp",EDGE,"E68.right")])]});
            var Q5;
            Q5=makeQuery(id+"F27.opExtrude","SWEPT_EDGE",EDGE,{"disambiguationData":[OSD([sQuery(id+"F26.wireOp",EDGE,"E68.bottom"),sQuery(id+"F26.wireOp",EDGE,"E68.left")])]});
            var Q6;
            Q6=makeQuery(id+"F27.opExtrude","SWEPT_EDGE",EDGE,{"disambiguationData":[OSD([sQuery(id+"F26.wireOp",EDGE,"E68.top"),sQuery(id+"F26.wireOp",EDGE,"E68.left")])]});
            var Q7;
            Q7=makeQuery(id+"F27.opExtrude","SWEPT_EDGE",EDGE,{"disambiguationData":[OSD([sQuery(id+"F26.wireOp",EDGE,"E68.top"),sQuery(id+"F26.wireOp",EDGE,"E68.right")])]});
            fillet(context, id + "F28", {"entities" : qUnion([Q0, Q1, Q2, Q3, Q4, Q5, Q6, Q7]), "radius" : 0.08 * mm, "tangentPropagation" : true, "allowEdgeOverflow" : false});
        }
        {
            var Q0;
            Q0=makeQuery(id+"F27.opExtrude","SWEPT_EDGE",EDGE,{"disambiguationData":[OSD([sQuery(id+"F26.wireOp",EDGE,"E69.top"),sQuery(id+"F26.wireOp",EDGE,"E69.right")])]});
            var Q1;
            Q1=makeQuery(id+"F27.opExtrude","SWEPT_EDGE",EDGE,{"disambiguationData":[OSD([sQuery(id+"F26.wireOp",EDGE,"E70.top"),sQuery(id+"F26.wireOp",EDGE,"E70.right")])]});
            var Q2;
            Q2=makeQuery(id+"F27.opExtrude","SWEPT_EDGE",EDGE,{"disambiguationData":[OSD([sQuery(id+"F26.wireOp",EDGE,"E69.top"),sQuery(id+"F26.wireOp",EDGE,"E69.left")])]});
            var Q3;
            Q3=makeQuery(id+"F27.opExtrude","SWEPT_EDGE",EDGE,{"disambiguationData":[OSD([sQuery(id+"F26.wireOp",EDGE,"E70.top"),sQuery(id+"F26.wireOp",EDGE,"E70.left")])]});
            var Q4;
            Q4=makeQuery(id+"F27.opExtrude","SWEPT_EDGE",EDGE,{"disambiguationData":[OSD([sQuery(id+"F26.wireOp",EDGE,"E69.bottom"),sQuery(id+"F26.wireOp",EDGE,"E69.left")])]});
            var Q5;
            Q5=makeQuery(id+"F27.opExtrude","SWEPT_EDGE",EDGE,{"disambiguationData":[OSD([sQuery(id+"F26.wireOp",EDGE,"E69.bottom"),sQuery(id+"F26.wireOp",EDGE,"E69.right")])]});
            var Q6;
            Q6=makeQuery(id+"F27.opExtrude","SWEPT_EDGE",EDGE,{"disambiguationData":[OSD([sQuery(id+"F26.wireOp",EDGE,"E70.bottom"),sQuery(id+"F26.wireOp",EDGE,"E70.left")])]});
            var Q7;
            Q7=makeQuery(id+"F27.opExtrude","SWEPT_EDGE",EDGE,{"disambiguationData":[OSD([sQuery(id+"F26.wireOp",EDGE,"E70.bottom"),sQuery(id+"F26.wireOp",EDGE,"E70.right")])]});
            fillet(context, id + "F29", {"entities" : qUnion([Q0, Q1, Q2, Q3, Q4, Q5, Q6, Q7]), "radius" : 0.15 * mm, "tangentPropagation" : true, "allowEdgeOverflow" : false});
        }
    });
